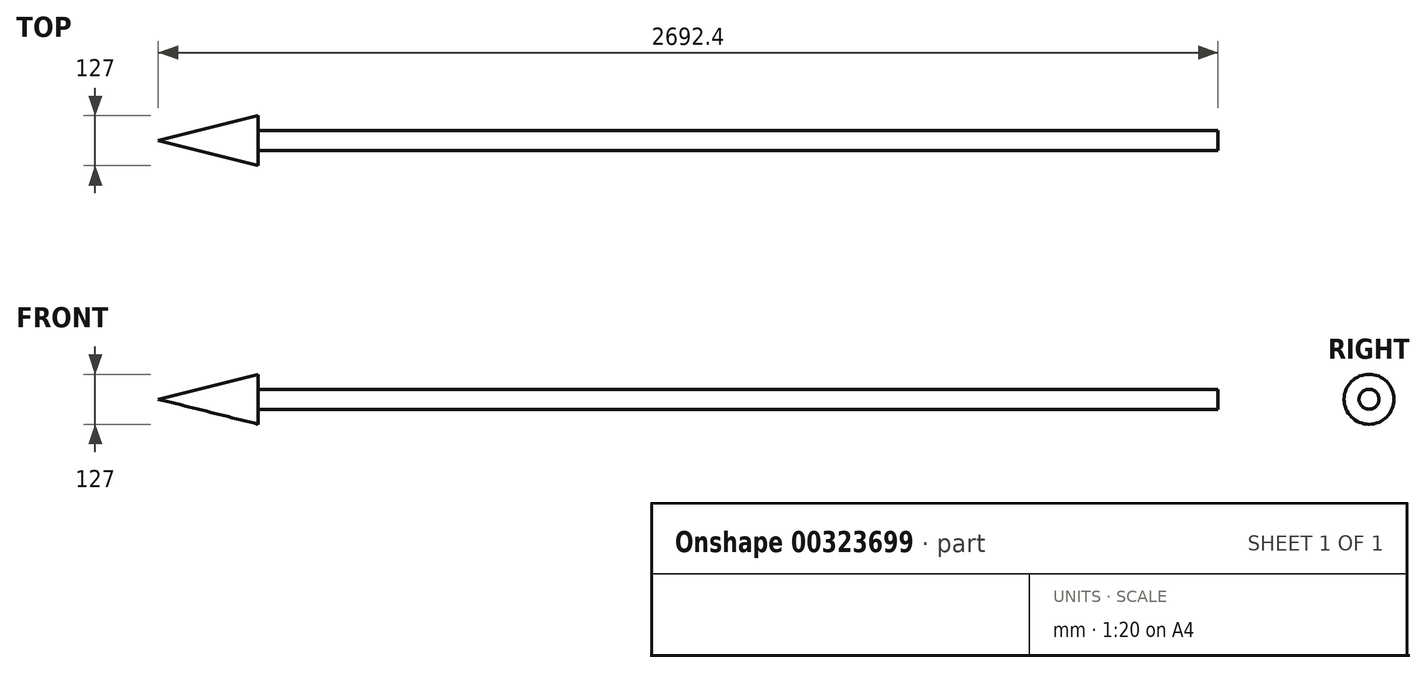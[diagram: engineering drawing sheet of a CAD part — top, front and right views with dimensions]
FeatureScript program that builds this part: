
annotation { "Feature Type Name" : "Feature", "Feature Type Description" : "" }
export const myFeature = defineFeature(function(context is Context, id is Id, definition is map)
    precondition{}
    {
        {
            var Q0;
            Q0=qCreatedBy(makeId("Right.planeOp"),FACE);
            var sketch = newSketch(context, id + "F0", { "sketchPlane" : qUnion([Q0])});
            skCircle(sketch, "E0", {"center": v(0, 0) * mm, "radius": 25.4 * mm});
            skSolve(sketch);
        }
        {
            var Q0;
            Q0=makeQuery(id+"F0.imprint","IMPRINT",FACE,{"disambiguationData":[TD([[makeQuery(id+"F0.imprint","IMPRINT",EDGE,{"derivedFrom":sQuery(id+"F0.wireOp",EDGE,"E0")}),1.0]])]});
            extrude(context, id + "F1", {"entities" : qUnion([Q0]), "depth" : 2438.4 * mm});
        }
        {
            var Q0;
            Q0=qCreatedBy(makeId("Right.planeOp"),FACE);
            var sketch = newSketch(context, id + "F2", { "sketchPlane" : qUnion([Q0])});
            skCircle(sketch, "E1", {"center": v(0, 0) * mm, "radius": 63.5 * mm});
            skSolve(sketch);
        }
        {
            var Q0;
            Q0=qCreatedBy(makeId("Right.planeOp"),FACE);
            cPlane(context, id + "F3", {"entities" : qUnion([Q0]), "cplaneType" : CPlaneType.OFFSET, "offset" : 254 * mm, "oppositeDirection" : true, "width" : 152.4 * mm, "height" : 152.4 * mm});
        }
        {
            var Q0;
            Q0=qCreatedBy(id+"F3.planeOp",FACE);
            var sketch = newSketch(context, id + "F4", { "sketchPlane" : qUnion([Q0])});
            skCircle(sketch, "E2", {"center": v(0, 0) * mm, "radius": 55.89 * mm});
            skSolve(sketch);
        }
        {
            var Q1;
            Q1=makeQuery(id+"F2.imprint","IMPRINT",FACE,{"disambiguationData":[TD([[makeQuery(id+"F2.imprint","IMPRINT",EDGE,{"derivedFrom":sQuery(id+"F2.wireOp",EDGE,"E1")}),1.0]])]});
            var Q2;
            Q2=sQuery(id+"F4.wireOp",VERTEX,"E2.center");
            loft(context, id + "F5", {"operationType" : NewBodyOperationType.ADD, "sheetProfilesArray" : [{ "sheetProfileEntities" : qUnion([Q1]) }, { "sheetProfileEntities" : qUnion([Q2]) }]});
        }
    });
